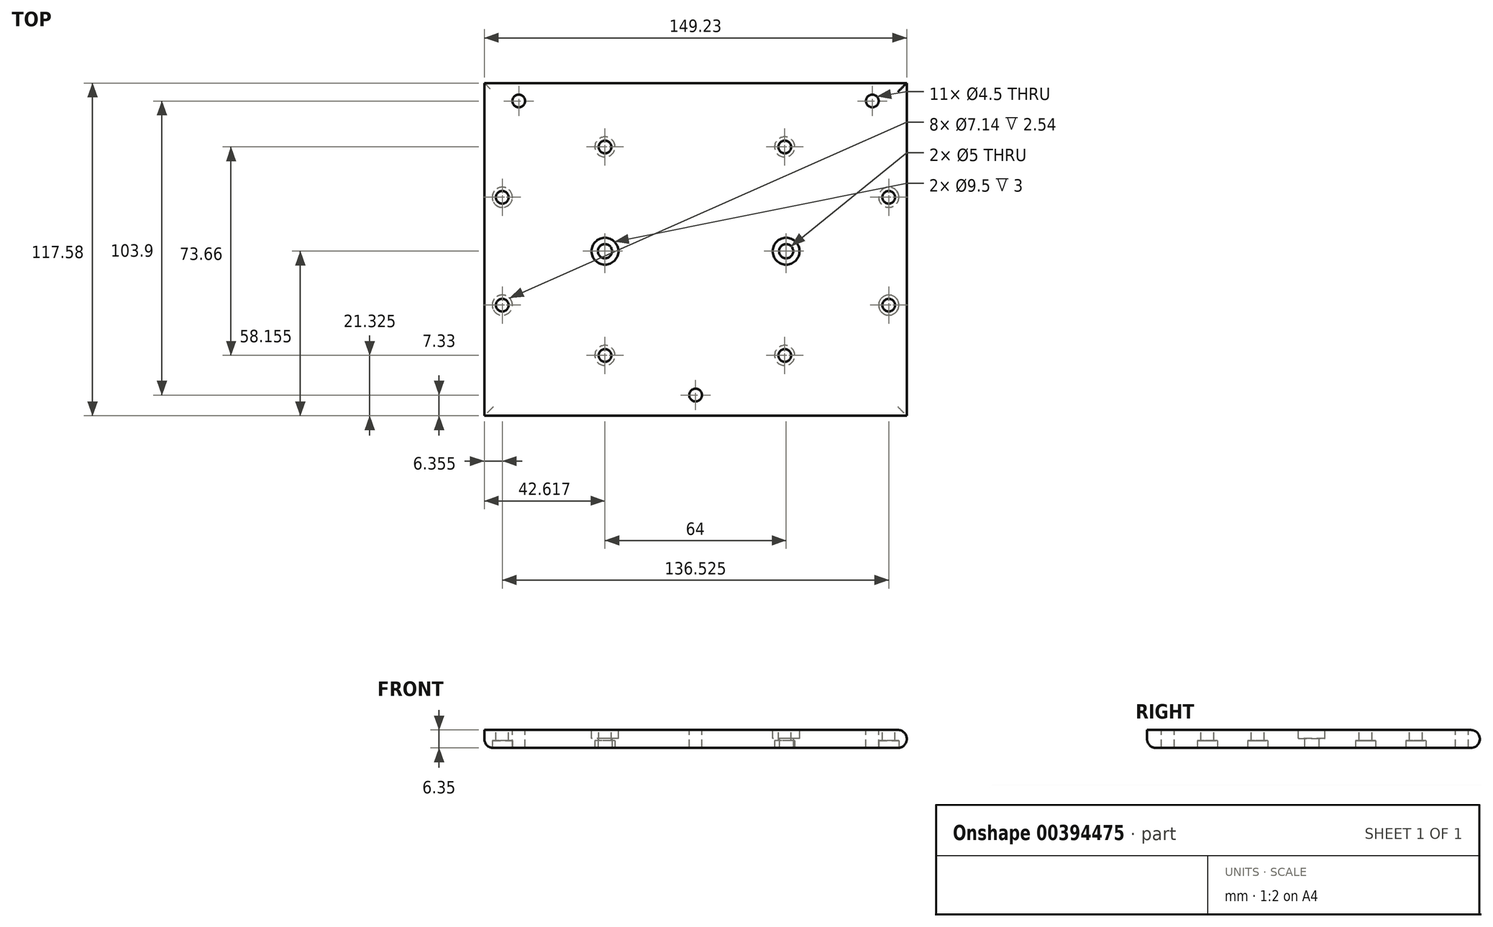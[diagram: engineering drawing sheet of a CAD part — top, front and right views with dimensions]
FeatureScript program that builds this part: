
annotation { "Feature Type Name" : "Feature", "Feature Type Description" : "" }
export const myFeature = defineFeature(function(context is Context, id is Id, definition is map)
    precondition{}
    {
        {
            var Q0;
            Q0=qCreatedBy(makeId("Top.planeOp"),FACE);
            var sketch = newSketch(context, id + "F0", { "sketchPlane" : qUnion([Q0])});
            skLineSegment(sketch, "E0.bottom", {"start": v(0, 0) * mm, "end": v(152.4, 0) * mm});
            skLineSegment(sketch, "E0.top", {"start": v(0, 127) * mm, "end": v(152.4, 127) * mm});
            skLineSegment(sketch, "E0.left", {"start": v(0, 0) * mm, "end": v(0, 127) * mm});
            skLineSegment(sketch, "E0.right", {"start": v(152.4, 0) * mm, "end": v(152.4, 127) * mm});
            skSolve(sketch);
        }
        {
            var Q0;
            Q0 = qSketchRegion(id + "F0", true);
            extrude(context, id + "F1", {"entities" : qUnion([Q0]), "depth" : 6.35 * mm});
        }
        {
            var Q0;
            {var subQ0=sQuery(id+"F0.wireOp",EDGE,"E0.left");var subQ1=sQuery(id+"F0.wireOp",EDGE,"E0.top");var subQ2=sQuery(id+"F0.wireOp",EDGE,"E0.bottom");Q0=makeQuery(id+"Fa2DmUKwfU0EPcb_1.boolean.opBoolean","SPLIT",FACE,{"disambiguationData":[TD([makeQuery(id+"F1.opExtrude","SWEPT_FACE",FACE,{"disambiguationData":[OSD([subQ0])]})])],"derivedFrom":makeQuery(id+"F1.opExtrude","CAP_FACE",FACE,{"disambiguationData":[OSD([subQ2,subQ1,subQ0,sQuery(id+"F0.wireOp",EDGE,"E0.right")])],"isStart":false})});}
            var sketch = newSketch(context, id + "F2", { "sketchPlane" : qUnion([Q0])});
            skCircle(sketch, "E1", {"center": v(15.34, 120.65) * mm, "radius": 2.25 * mm});
            skCircle(sketch, "E2", {"center": v(140.24, 120.65) * mm, "radius": 2.25 * mm});
            skCircle(sketch, "E3", {"center": v(77.79, 16.75) * mm, "radius": 2.25 * mm});
            skLineSegment(sketch, "E4", {"start": v(15.34, 120.65) * mm, "end": v(140.24, 120.65) * mm, "construction": true});
            skLineSegment(sketch, "E5", {"start": v(77.79, 16.75) * mm, "end": v(77.79, 120.65) * mm, "construction": true});
            skPoint(sketch, "E6", {"position": v(77.79, 120.65) * mm});
            skLineSegment(sketch, "E7", {"start": v(152.4, 68.84) * mm, "end": v(77.79, 68.84) * mm, "construction": true});
            skSolve(sketch);
        }
        {
            var Q0;
            Q0 = qSketchRegion(id + "F2", true);
            extrude(context, id + "F3", {"entities" : qUnion([Q0]), "operationType" : NewBodyOperationType.REMOVE, "endBound" : BoundingType.THROUGH_ALL, "oppositeDirection" : true, "depth" : 25.4 * mm});
        }
        {
            var Q0;
            Q0=makeQuery(id+"F1.opExtrude","CAP_FACE",FACE,{"disambiguationData":[OSD([sQuery(id+"F0.wireOp",EDGE,"E0.bottom"),sQuery(id+"F0.wireOp",EDGE,"E0.top"),sQuery(id+"F0.wireOp",EDGE,"E0.left"),sQuery(id+"F0.wireOp",EDGE,"E0.right")])],"isStart":true});
            var sketch = newSketch(context, id + "F4", { "sketchPlane" : qUnion([Q0])});
            skLineSegment(sketch, "E8", {"start": v(77.79, -14.5) * mm, "end": v(77.79, -120.65) * mm, "construction": true});
            skCircle(sketch, "E9", {"center": v(45.79, -67.58) * mm, "radius": 2.5 * mm});
            skCircle(sketch, "E10", {"center": v(109.79, -67.58) * mm, "radius": 2.5 * mm});
            skPoint(sketch, "E11", {"position": v(77.79, -67.58) * mm});
            skLineSegment(sketch, "E12", {"start": v(15.34, -120.65) * mm, "end": v(140.24, -120.65) * mm, "construction": true});
            skSolve(sketch);
        }
        {
            var Q0;
            Q0 = qSketchRegion(id + "F4", true);
            extrude(context, id + "F5", {"entities" : qUnion([Q0]), "operationType" : NewBodyOperationType.REMOVE, "oppositeDirection" : true, "depth" : 25.4 * mm});
        }
        {
            var Q0;
            Q0=makeQuery(id+"F1.opExtrude","CAP_FACE",FACE,{"disambiguationData":[OSD([sQuery(id+"F0.wireOp",EDGE,"E0.bottom"),sQuery(id+"F0.wireOp",EDGE,"E0.top"),sQuery(id+"F0.wireOp",EDGE,"E0.left"),sQuery(id+"F0.wireOp",EDGE,"E0.right")])],"isStart":false});
            var sketch = newSketch(context, id + "F6", { "sketchPlane" : qUnion([Q0])});
            skCircle(sketch, "E13", {"center": v(45.79, 67.58) * mm, "radius": 4.75 * mm});
            skCircle(sketch, "E14", {"center": v(109.79, 67.58) * mm, "radius": 4.75 * mm});
            skSolve(sketch);
        }
        {
            var Q0;
            Q0 = qSketchRegion(id + "F6", true);
            extrude(context, id + "F7", {"entities" : qUnion([Q0]), "operationType" : NewBodyOperationType.REMOVE, "oppositeDirection" : true, "depth" : 3 * mm});
        }
        {
            var Q0;
            Q0=makeQuery(id+"F1.opExtrude","CAP_FACE",FACE,{"disambiguationData":[OSD([sQuery(id+"F0.wireOp",EDGE,"E0.bottom"),sQuery(id+"F0.wireOp",EDGE,"E0.top"),sQuery(id+"F0.wireOp",EDGE,"E0.left"),sQuery(id+"F0.wireOp",EDGE,"E0.right")])],"isStart":false});
            var sketch = newSketch(context, id + "F8", { "sketchPlane" : qUnion([Q0])});
            skCircle(sketch, "E15", {"center": v(146.05, 86.62) * mm, "radius": 2.25 * mm});
            skCircle(sketch, "E16", {"center": v(146.05, 48.53) * mm, "radius": 2.25 * mm});
            skCircle(sketch, "E17", {"center": v(9.53, 48.52) * mm, "radius": 2.25 * mm});
            skCircle(sketch, "E18", {"center": v(9.52, 86.62) * mm, "radius": 2.25 * mm});
            skCircle(sketch, "E19", {"center": v(45.79, 104.4) * mm, "radius": 2.25 * mm});
            skCircle(sketch, "E20", {"center": v(109.29, 104.4) * mm, "radius": 2.25 * mm});
            skCircle(sketch, "E21", {"center": v(45.79, 30.74) * mm, "radius": 2.25 * mm});
            skCircle(sketch, "E22", {"center": v(109.29, 30.75) * mm, "radius": 2.25 * mm});
            skLineSegment(sketch, "E23", {"start": v(45.79, 67.58) * mm, "end": v(109.79, 67.58) * mm, "construction": true});
            skLineSegment(sketch, "E24", {"start": v(45.79, 104.4) * mm, "end": v(45.79, 30.74) * mm, "construction": true});
            skLineSegment(sketch, "E25", {"start": v(9.52, 86.62) * mm, "end": v(9.53, 48.52) * mm, "construction": true});
            skPoint(sketch, "E26", {"position": v(9.52, 67.57) * mm});
            skSolve(sketch);
        }
        {
            var Q0;
            Q0 = qSketchRegion(id + "F8", true);
            extrude(context, id + "F9", {"entities" : qUnion([Q0]), "operationType" : NewBodyOperationType.REMOVE, "endBound" : BoundingType.THROUGH_ALL, "oppositeDirection" : true, "depth" : 25.4 * mm});
        }
        {
            var Q0;
            Q0=makeQuery(id+"F1.opExtrude","CAP_FACE",FACE,{"disambiguationData":[OSD([sQuery(id+"F0.wireOp",EDGE,"E0.bottom"),sQuery(id+"F0.wireOp",EDGE,"E0.top"),sQuery(id+"F0.wireOp",EDGE,"E0.left"),sQuery(id+"F0.wireOp",EDGE,"E0.right")])],"isStart":false});
            var sketch = newSketch(context, id + "F10", { "sketchPlane" : qUnion([Q0])});
            skLineSegment(sketch, "E27.bottom", {"start": v(0, 0) * mm, "end": v(3.17, 0) * mm});
            skLineSegment(sketch, "E27.top", {"start": v(0, 127) * mm, "end": v(3.17, 127) * mm});
            skLineSegment(sketch, "E27.left", {"start": v(0, 0) * mm, "end": v(0, 127) * mm});
            skLineSegment(sketch, "E27.right", {"start": v(3.17, 0) * mm, "end": v(3.17, 127) * mm});
            skLineSegment(sketch, "E28.bottom", {"start": v(0, 0) * mm, "end": v(152.4, 0) * mm});
            skLineSegment(sketch, "E28.top", {"start": v(0, 9.42) * mm, "end": v(152.4, 9.42) * mm});
            skLineSegment(sketch, "E28.left", {"start": v(0, 0) * mm, "end": v(0, 9.42) * mm});
            skLineSegment(sketch, "E28.right", {"start": v(152.4, 0) * mm, "end": v(152.4, 9.42) * mm});
            skPoint(sketch, "E29", {"position": v(9.52, 86.62) * mm});
            skSolve(sketch);
        }
        {
            var Q0;
            Q0 = qSketchRegion(id + "F10", true);
            extrude(context, id + "F11", {"entities" : qUnion([Q0]), "operationType" : NewBodyOperationType.REMOVE, "endBound" : BoundingType.THROUGH_ALL, "oppositeDirection" : true, "depth" : 25.4 * mm});
        }
        {
            var Q0;
            Q0=makeQuery(id+"F11.boolean.opBoolean","COPY",EDGE,{"derivedFrom":makeQuery(id+"F11.opExtrude","CAP_EDGE",EDGE,{"disambiguationData":[OSD([sQuery(id+"F10.wireOp",EDGE,"E27.right")])],"isStart":true})});
            var Q1;
            Q1=makeQuery(id+"F11.boolean.opBoolean","COPY",EDGE,{"derivedFrom":makeQuery(id+"F11.opExtrude","CAP_EDGE",EDGE,{"disambiguationData":[OSD([sQuery(id+"F10.wireOp",EDGE,"E28.top")])],"isStart":true})});
            var Q2;
            Q2=makeQuery(id+"F1.opExtrude","CAP_EDGE",EDGE,{"disambiguationData":[OSD([sQuery(id+"F0.wireOp",EDGE,"E0.right")])],"isStart":false});
            var Q3;
            Q3=makeQuery(id+"F1.opExtrude","CAP_EDGE",EDGE,{"disambiguationData":[OSD([sQuery(id+"F0.wireOp",EDGE,"E0.top")])],"isStart":false});
            var Q4;
            Q4=makeQuery(id+"F1.opExtrude","CAP_EDGE",EDGE,{"disambiguationData":[OSD([sQuery(id+"F0.wireOp",EDGE,"E0.top")])],"isStart":true});
            var Q5;
            Q5=makeQuery(id+"F11.boolean.opBoolean","INTERSECT",EDGE,{"derivedFrom":[makeQuery(id+"F1.opExtrude","CAP_FACE",FACE,{"disambiguationData":[OSD([sQuery(id+"F0.wireOp",EDGE,"E0.bottom"),sQuery(id+"F0.wireOp",EDGE,"E0.top"),sQuery(id+"F0.wireOp",EDGE,"E0.left"),sQuery(id+"F0.wireOp",EDGE,"E0.right")])],"isStart":true}),makeQuery(id+"F11.opExtrude","SWEPT_FACE",FACE,{"disambiguationData":[OSD([sQuery(id+"F10.wireOp",EDGE,"E27.right")])]})]});
            var Q6;
            Q6=makeQuery(id+"F11.boolean.opBoolean","INTERSECT",EDGE,{"derivedFrom":[makeQuery(id+"F1.opExtrude","CAP_FACE",FACE,{"disambiguationData":[OSD([sQuery(id+"F0.wireOp",EDGE,"E0.bottom"),sQuery(id+"F0.wireOp",EDGE,"E0.top"),sQuery(id+"F0.wireOp",EDGE,"E0.left"),sQuery(id+"F0.wireOp",EDGE,"E0.right")])],"isStart":true}),makeQuery(id+"F11.opExtrude","SWEPT_FACE",FACE,{"disambiguationData":[OSD([sQuery(id+"F10.wireOp",EDGE,"E28.top")])]})]});
            var Q7;
            Q7=makeQuery(id+"F1.opExtrude","CAP_EDGE",EDGE,{"disambiguationData":[OSD([sQuery(id+"F0.wireOp",EDGE,"E0.right")])],"isStart":true});
            fillet(context, id + "F12", {"entities" : qUnion([Q0, Q1, Q2, Q3, Q4, Q5, Q6, Q7]), "radius" : 3.17 * mm, "tangentPropagation" : true, "allowEdgeOverflow" : false});
        }
        {
            var Q0;
            Q0=makeQuery(id+"F0.imprint","IMPRINT",FACE,{"disambiguationData":[TD([[makeQuery(id+"F0.imprint","IMPRINT",EDGE,{"derivedFrom":sQuery(id+"F0.wireOp",EDGE,"E0.bottom")}),1.0]])]});
            var sketch = newSketch(context, id + "F13", { "sketchPlane" : qUnion([Q0])});
            skCircle(sketch, "E30", {"center": v(45.79, 30.74) * mm, "radius": 3.57 * mm});
            skCircle(sketch, "E31", {"center": v(109.29, 30.75) * mm, "radius": 3.57 * mm});
            skCircle(sketch, "E32", {"center": v(9.53, 48.52) * mm, "radius": 3.57 * mm});
            skCircle(sketch, "E33", {"center": v(9.52, 86.62) * mm, "radius": 3.57 * mm});
            skCircle(sketch, "E34", {"center": v(45.79, 104.4) * mm, "radius": 3.57 * mm});
            skCircle(sketch, "E35", {"center": v(109.29, 104.4) * mm, "radius": 3.57 * mm});
            skCircle(sketch, "E36", {"center": v(146.05, 86.62) * mm, "radius": 3.57 * mm});
            skCircle(sketch, "E37", {"center": v(146.05, 48.53) * mm, "radius": 3.57 * mm});
            skSolve(sketch);
        }
        {
            var Q0;
            Q0 = qSketchRegion(id + "F13", true);
            extrude(context, id + "F14", {"entities" : qUnion([Q0]), "operationType" : NewBodyOperationType.REMOVE, "depth" : 2.54 * mm});
        }
    });
